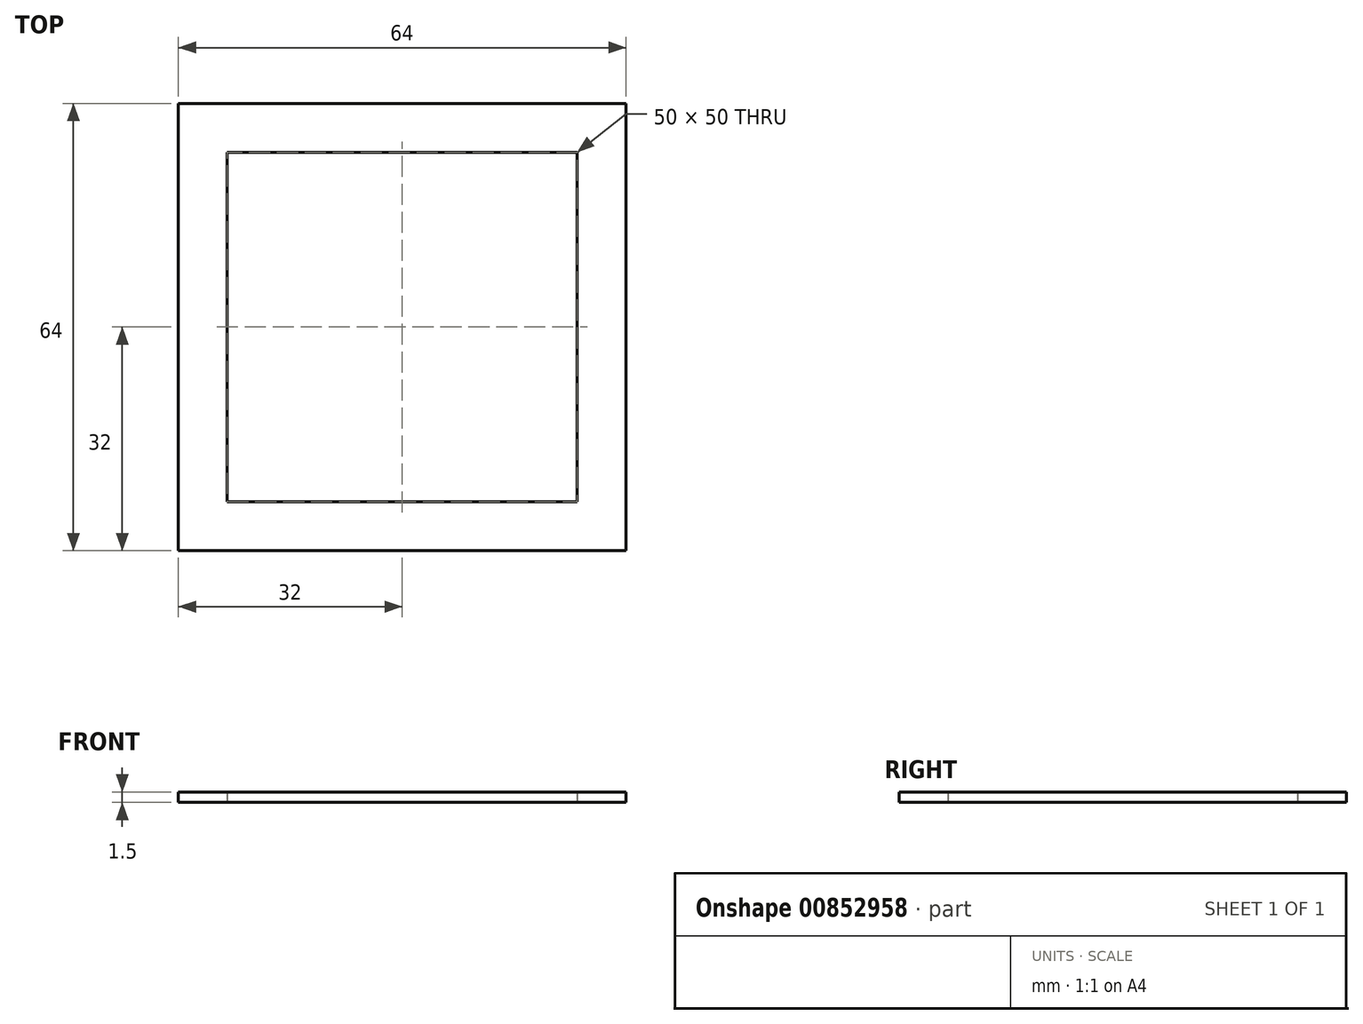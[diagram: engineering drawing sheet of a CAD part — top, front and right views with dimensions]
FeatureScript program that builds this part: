
annotation { "Feature Type Name" : "Feature", "Feature Type Description" : "" }
export const myFeature = defineFeature(function(context is Context, id is Id, definition is map)
    precondition{}
    {
        {
            var Q0;
            Q0=qCreatedBy(makeId("Top.planeOp"),FACE);
            var sketch = newSketch(context, id + "F0", { "sketchPlane" : qUnion([Q0])});
            skLineSegment(sketch, "E0.bottom", {"start": v(-32, 32) * mm, "end": v(32, 32) * mm});
            skLineSegment(sketch, "E0.top", {"start": v(-32, -32) * mm, "end": v(32, -32) * mm});
            skLineSegment(sketch, "E0.left", {"start": v(-32, 32) * mm, "end": v(-32, -32) * mm});
            skLineSegment(sketch, "E0.right", {"start": v(32, 32) * mm, "end": v(32, -32) * mm});
            skPoint(sketch, "E0.middle", {"position": v(0, 0) * mm});
            skSolve(sketch);
        }
        {
            var Q0;
            Q0 = qSketchRegion(id + "F0", true);
            extrude(context, id + "F1", {"entities" : qUnion([Q0]), "depth" : 1.5 * mm, "offsetDistance" : 25 * mm});
        }
        {
            var Q0;
            Q0=qCreatedBy(makeId("Top.planeOp"),FACE);
            var sketch = newSketch(context, id + "F2", { "sketchPlane" : qUnion([Q0])});
            skLineSegment(sketch, "E1.bottom", {"start": v(-25, 25) * mm, "end": v(25, 25) * mm});
            skLineSegment(sketch, "E1.top", {"start": v(-25, -25) * mm, "end": v(25, -25) * mm});
            skLineSegment(sketch, "E1.left", {"start": v(-25, 25) * mm, "end": v(-25, -25) * mm});
            skLineSegment(sketch, "E1.right", {"start": v(25, 25) * mm, "end": v(25, -25) * mm});
            skPoint(sketch, "E1.middle", {"position": v(0, 0) * mm});
            skSolve(sketch);
        }
        {
            var Q0;
            Q0 = qSketchRegion(id + "F2", true);
            extrude(context, id + "F3", {"entities" : qUnion([Q0]), "operationType" : NewBodyOperationType.REMOVE, "endBound" : BoundingType.THROUGH_ALL, "depth" : 25 * mm, "offsetDistance" : 25 * mm});
        }
    });
